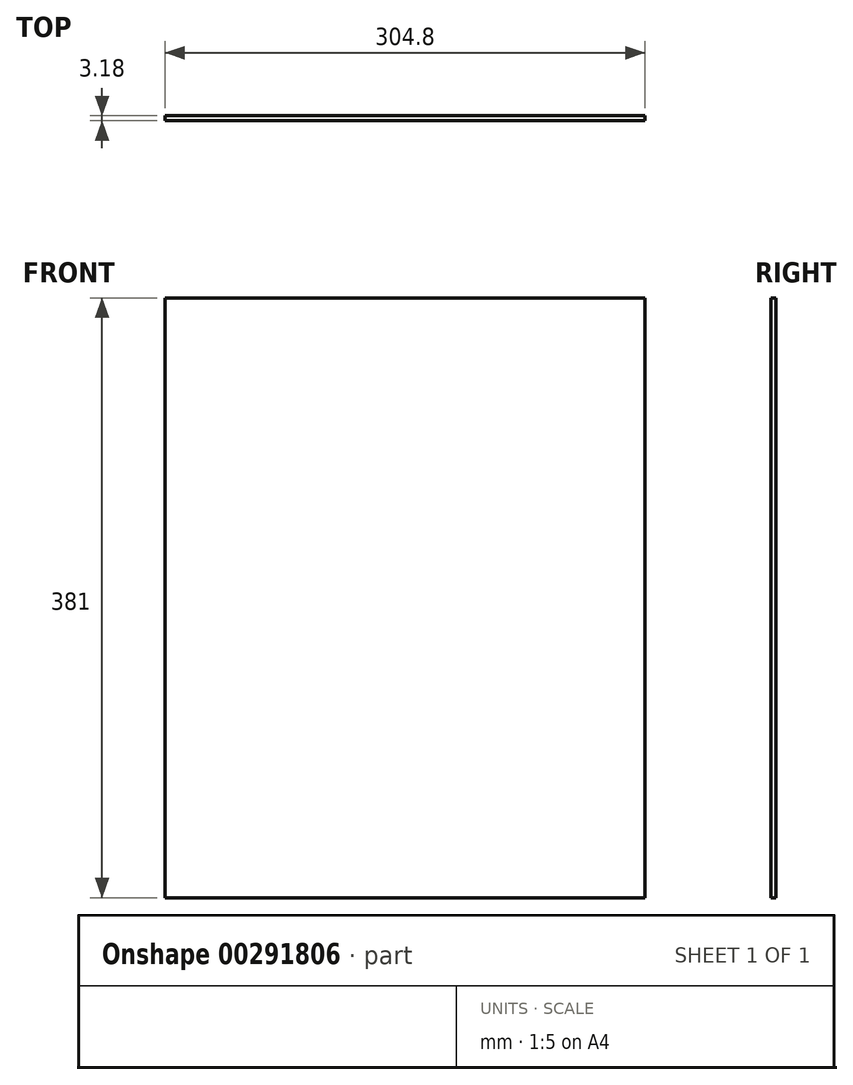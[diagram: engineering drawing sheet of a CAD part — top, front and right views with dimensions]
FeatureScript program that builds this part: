
annotation { "Feature Type Name" : "Feature", "Feature Type Description" : "" }
export const myFeature = defineFeature(function(context is Context, id is Id, definition is map)
    precondition{}
    {
        {
            var Q0;
            Q0=qCreatedBy(makeId("Front.planeOp"),FACE);
            var sketch = newSketch(context, id + "F0", { "sketchPlane" : qUnion([Q0])});
            skLineSegment(sketch, "E0.bottom", {"start": v(152.4, 190.5) * mm, "end": v(-152.4, 190.5) * mm});
            skLineSegment(sketch, "E0.top", {"start": v(152.4, -190.5) * mm, "end": v(-152.4, -190.5) * mm});
            skLineSegment(sketch, "E0.left", {"start": v(152.4, 190.5) * mm, "end": v(152.4, -190.5) * mm});
            skLineSegment(sketch, "E0.right", {"start": v(-152.4, 190.5) * mm, "end": v(-152.4, -190.5) * mm});
            skPoint(sketch, "E0.middle", {"position": v(0, 0) * mm});
            skSolve(sketch);
        }
        {
            var Q0;
            Q0 = qSketchRegion(id + "F0", true);
            extrude(context, id + "F1", {"entities" : qUnion([Q0]), "endBound" : BoundingType.SYMMETRIC, "depth" : 3.17 * mm});
        }
    });
